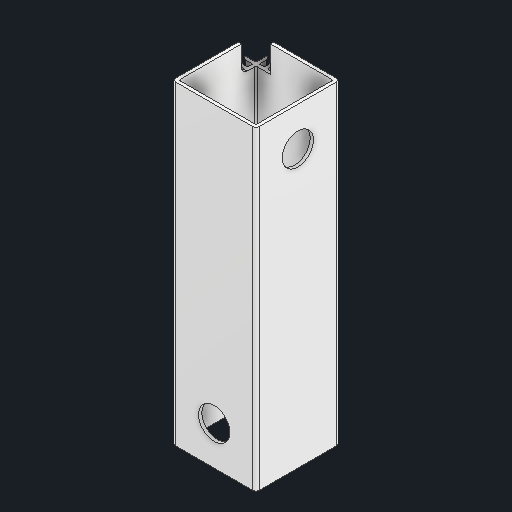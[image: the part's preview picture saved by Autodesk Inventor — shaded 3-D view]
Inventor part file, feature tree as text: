
AUTODESK INVENTOR PART (.ipt)
format: ipt  version: 2025 (Build 290162000, 162)  size: 143,872 bytes
history: native  units: in
note: dims shown in document units (in); Inventor stores cm internally (conversion verified against a paired STEP export)
features: fillet x1
ambient origin geometry x8: Origin, YZ Plane, XZ Plane, XY Plane, X Axis, Y Axis, Z Axis, Center Point
bodies: Solid1 (feature_tree)
feature tree (1):
  fillet  "Fillet5"  [1 undecoded]
note: 1 required parameter value undecoded (feature->parameter linkage not recoverable at this tier; creation-order binding heuristic only, values carry confidence <= 0.55)
